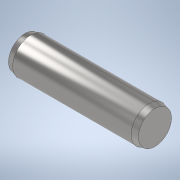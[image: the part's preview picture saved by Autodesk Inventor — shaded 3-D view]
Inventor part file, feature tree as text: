
AUTODESK INVENTOR PART (.ipt)
format: ipt  version: 2022 (Build 260153000, 153)  size: 111,104 bytes
history: native  units: in
note: dims shown in document units (in); Inventor stores cm internally (conversion verified against a paired STEP export)
features: extrude x1
ambient origin geometry x8: Origin, YZ Plane, XZ Plane, XY Plane, X Axis, Y Axis, Z Axis, Center Point
bodies: Solid1 (feature_tree)
feature tree (1):
  extrude  "Extrude3"  [1 undecoded]
note: 1 required parameter value undecoded (feature->parameter linkage not recoverable at this tier; creation-order binding heuristic only, values carry confidence <= 0.55)
